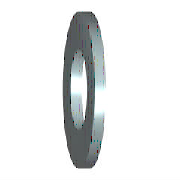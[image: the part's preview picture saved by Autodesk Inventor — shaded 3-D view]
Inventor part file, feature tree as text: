
AUTODESK INVENTOR PART (.ipt)
format: ipt  version: 2015 (Build 190159000, 159)  size: 106,496 bytes
history: native  units: mm (DEFAULTED — no unit token found)
features: other x1, plane x1, sketch x1
ambient origin geometry x7: Origin, YZ Plane, XY Plane, X Axis, Y Axis, Z Axis, Center Point
bodies: Solid1 (feature_tree), Body (feature_tree)
feature tree (3):
  other  "Work Axis1"
  plane  "Work Plane1"
  sketch  "Sketch"  dims[d0=8.4mm d1=16.0mm d2=1.6mm d3=0.0mm d4=0.0mm d5=0.0mm d6=0.0mm d7=0.0mm]
